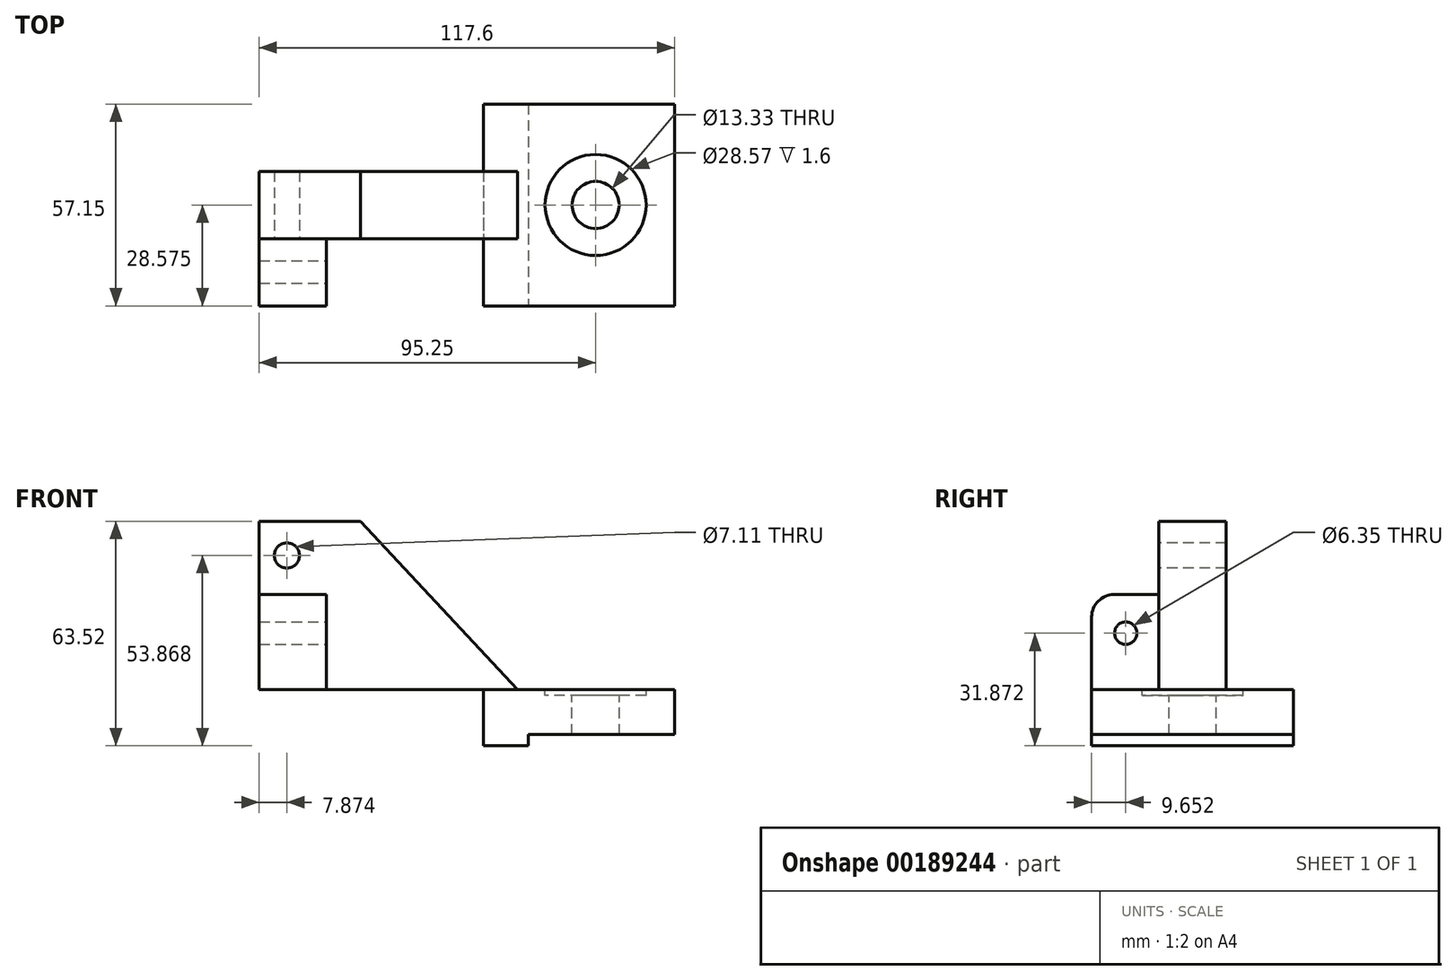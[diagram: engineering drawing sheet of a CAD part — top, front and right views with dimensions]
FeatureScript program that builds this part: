
annotation { "Feature Type Name" : "Feature", "Feature Type Description" : "" }
export const myFeature = defineFeature(function(context is Context, id is Id, definition is map)
    precondition{}
    {
        {
            var Q0;
            Q0=qCreatedBy(makeId("Front.planeOp"),FACE);
            var sketch = newSketch(context, id + "F0", { "sketchPlane" : qUnion([Q0])});
            skLineSegment(sketch, "E0.bottom", {"start": v(0, 0) * mm, "end": v(41.4, 0) * mm});
            skLineSegment(sketch, "E0.top", {"start": v(0, 12.7) * mm, "end": v(41.4, 12.7) * mm});
            skLineSegment(sketch, "E0.left", {"start": v(0, 0) * mm, "end": v(0, 12.7) * mm});
            skLineSegment(sketch, "E0.right", {"start": v(41.4, 0) * mm, "end": v(41.4, 12.7) * mm});
            skLineSegment(sketch, "E1.bottom", {"start": v(0, 12.7) * mm, "end": v(-12.7, 12.7) * mm});
            skLineSegment(sketch, "E1.top", {"start": v(0, -3.17) * mm, "end": v(-12.7, -3.17) * mm});
            skLineSegment(sketch, "E1.left", {"start": v(0, 12.7) * mm, "end": v(0, -3.17) * mm});
            skLineSegment(sketch, "E1.right", {"start": v(-12.7, 12.7) * mm, "end": v(-12.7, -3.18) * mm});
            skSolve(sketch);
        }
        {
            var Q0;
            Q0 = qSketchRegion(id + "F0", true);
            extrude(context, id + "F1", {"entities" : qUnion([Q0]), "oppositeDirection" : true, "depth" : 57.15 * mm});
        }
        {
            var Q0;
            Q0=makeQuery(id+"F1.opExtrude","SWEPT_FACE",FACE,{"disambiguationData":[OSD([sQuery(id+"F0.wireOp",EDGE,"E0.top"),sQuery(id+"F0.wireOp",EDGE,"E1.bottom")])]});
            var sketch = newSketch(context, id + "F2", { "sketchPlane" : qUnion([Q0])});
            skLineSegment(sketch, "E2", {"start": v(41.4, 28.58) * mm, "end": v(41.4, 0) * mm});
            skLineSegment(sketch, "E3", {"start": v(41.4, 28.58) * mm, "end": v(19.05, 28.58) * mm});
            skPoint(sketch, "E4", {"position": v(19.05, 28.58) * mm});
            skLineSegment(sketch, "E5", {"start": v(41.4, 28.58) * mm, "end": v(-3.05, 28.58) * mm});
            skLineSegment(sketch, "E6.bottom", {"start": v(-3.05, 19.05) * mm, "end": v(-47.5, 19.05) * mm});
            skLineSegment(sketch, "E6.top", {"start": v(-3.05, 38.1) * mm, "end": v(-47.5, 38.1) * mm});
            skLineSegment(sketch, "E6.left", {"start": v(-3.05, 19.05) * mm, "end": v(-3.05, 38.1) * mm});
            skLineSegment(sketch, "E6.right", {"start": v(-47.5, 19.05) * mm, "end": v(-47.5, 38.1) * mm});
            skSolve(sketch);
        }
        {
            var Q0;
            Q0=sQuery(id+"F2.wireOp",VERTEX,"E4");
            var Q1;
            Q1=makeQuery(id+"F1.opExtrude","SWEPT_BODY",BODY,{"disambiguationData":[OSD([sQuery(id+"F0.wireOp",EDGE,"E0.bottom"),sQuery(id+"F0.wireOp",EDGE,"E0.top"),sQuery(id+"F0.wireOp",EDGE,"E0.right"),sQuery(id+"F0.wireOp",EDGE,"E1.bottom"),sQuery(id+"F0.wireOp",EDGE,"E1.top"),sQuery(id+"F0.wireOp",EDGE,"E1.left"),sQuery(id+"F0.wireOp",EDGE,"E1.right")])]});
            hole(context, id + "F3", {"style" : HoleStyle.C_BORE, "endStyle" : HoleEndStyle.THROUGH, "standardTappedOrClearance" : lookupTablePath({ "standard" : "ANSI", "fit" : "Normal (ASME)", "size" : "1/4", "type" : "Clearance" }), "standardBlindInLast" : lookupTablePath({ "fit" : "Free", "standard" : "ANSI", "size" : "1/4", "type" : "Clearance" }), "holeDiameter" : 13.33 * mm, "cBoreDiameter" : 28.57 * mm, "cBoreDepth" : 1.6 * mm, "startFromSketch" : true, "locations" : qUnion([Q0]), "scope" : qUnion([Q1]), "isTappedThrough" : true});
        }
        {
            var Q0;
            {var subQ0=sQuery(id+"F2.wireOp",EDGE,"E6.right");Q0=makeQuery(id+"F2.imprint","IMPRINT",FACE,{"disambiguationData":[TD([[makeQuery(id+"F2.imprint","IMPRINT",EDGE,{"derivedFrom":subQ0}),-1.0]])]});}
            var Q1;
            {var subQ0=sQuery(id+"F2.wireOp",EDGE,"E6.left");var subQ1=makeQuery(id+"F2.imprint","INTERSECT",VERTEX,{"derivedFrom":[sQuery(id+"F2.wireOp",EDGE,"E5"),subQ0]});Q1=makeQuery(id+"F2.imprint","IMPRINT",FACE,{"disambiguationData":[TD([[makeQuery(id+"F2.imprint","IMPRINT",EDGE,{"disambiguationData":[TD([[subQ1,1.0]])],"derivedFrom":subQ0}),1.0]])]});}
            extrude(context, id + "F4", {"entities" : qUnion([Q0, Q1]), "operationType" : NewBodyOperationType.ADD, "depth" : 47.65 * mm});
        }
        {
            var Q0;
            Q0=makeQuery(id+"F4.opExtrude","SWEPT_FACE",FACE,{"disambiguationData":[OSD([sQuery(id+"F2.wireOp",EDGE,"E6.bottom")])]});
            var sketch = newSketch(context, id + "F5", { "sketchPlane" : qUnion([Q0])});
            skLineSegment(sketch, "E7", {"start": v(-47.5, 60.35) * mm, "end": v(-3.05, 12.7) * mm});
            skLineSegment(sketch, "E8", {"start": v(-3.05, 12.7) * mm, "end": v(-3.05, 60.35) * mm});
            skLineSegment(sketch, "E9", {"start": v(-3.05, 60.35) * mm, "end": v(-47.5, 60.35) * mm});
            skSolve(sketch);
        }
        {
            var Q0;
            Q0 = qSketchRegion(id + "F5", true);
            extrude(context, id + "F6", {"entities" : qUnion([Q0]), "operationType" : NewBodyOperationType.REMOVE, "oppositeDirection" : true, "depth" : 34.95 * mm});
        }
        {
            var Q0;
            Q0=makeQuery(id+"F4.opExtrude","SWEPT_FACE",FACE,{"disambiguationData":[OSD([sQuery(id+"F2.wireOp",EDGE,"E6.right")])]});
            var sketch = newSketch(context, id + "F7", { "sketchPlane" : qUnion([Q0])});
            skLineSegment(sketch, "E10.bottom", {"start": v(-19.05, 12.7) * mm, "end": v(-38.1, 12.7) * mm});
            skLineSegment(sketch, "E10.top", {"start": v(-19.05, 60.35) * mm, "end": v(-38.1, 60.35) * mm});
            skLineSegment(sketch, "E10.left", {"start": v(-19.05, 12.7) * mm, "end": v(-19.05, 60.35) * mm});
            skLineSegment(sketch, "E10.right", {"start": v(-38.1, 12.7) * mm, "end": v(-38.1, 60.35) * mm});
            skSolve(sketch);
        }
        {
            var Q0;
            Q0 = qSketchRegion(id + "F7", true);
            extrude(context, id + "F8", {"entities" : qUnion([Q0]), "operationType" : NewBodyOperationType.ADD, "depth" : 28.7 * mm});
        }
        {
            var Q0;
            Q0=makeQuery(id+"F8.boolean.opBoolean","MERGE",FACE,{"derivedFrom":[makeQuery(id+"F4.opExtrude","SWEPT_FACE",FACE,{"disambiguationData":[OSD([sQuery(id+"F2.wireOp",EDGE,"E6.bottom")])]}),makeQuery(id+"F8.opExtrude","SWEPT_FACE",FACE,{"disambiguationData":[OSD([sQuery(id+"F7.wireOp",EDGE,"E10.left")])]})]});
            var sketch = newSketch(context, id + "F9", { "sketchPlane" : qUnion([Q0])});
            skLineSegment(sketch, "E11.bottom", {"start": v(-76.2, 12.7) * mm, "end": v(-57.15, 12.7) * mm});
            skLineSegment(sketch, "E11.top", {"start": v(-76.2, 39.62) * mm, "end": v(-57.15, 39.62) * mm});
            skLineSegment(sketch, "E11.left", {"start": v(-76.2, 12.7) * mm, "end": v(-76.2, 39.62) * mm});
            skLineSegment(sketch, "E11.right", {"start": v(-57.15, 12.7) * mm, "end": v(-57.15, 39.62) * mm});
            skSolve(sketch);
        }
        {
            var Q0;
            Q0 = qSketchRegion(id + "F9", true);
            extrude(context, id + "F10", {"entities" : qUnion([Q0]), "operationType" : NewBodyOperationType.ADD, "depth" : 19.05 * mm});
        }
        {
            var Q0;
            Q0=makeQuery(id+"F10.opExtrude","CAP_EDGE",EDGE,{"disambiguationData":[OSD([sQuery(id+"F9.wireOp",EDGE,"E11.top")])],"isStart":false});
            fillet(context, id + "F11", {"entities" : qUnion([Q0]), "radius" : 6.35 * mm, "tangentPropagation" : true, "allowEdgeOverflow" : false});
        }
        {
            var Q0;
            Q0=makeQuery(id+"F10.opExtrude","SWEPT_FACE",FACE,{"disambiguationData":[OSD([sQuery(id+"F9.wireOp",EDGE,"E11.right")])]});
            var sketch = newSketch(context, id + "F12", { "sketchPlane" : qUnion([Q0])});
            skLineSegment(sketch, "E12.bottom", {"start": v(0, 12.7) * mm, "end": v(9.65, 12.7) * mm});
            skLineSegment(sketch, "E12.top", {"start": v(0, 28.7) * mm, "end": v(9.65, 28.7) * mm});
            skLineSegment(sketch, "E12.left", {"start": v(0, 12.7) * mm, "end": v(0, 28.7) * mm});
            skLineSegment(sketch, "E12.right", {"start": v(9.65, 12.7) * mm, "end": v(9.65, 28.7) * mm});
            skPoint(sketch, "E13", {"position": v(9.65, 28.7) * mm});
            skSolve(sketch);
        }
        {
            var Q0;
            Q0=makeQuery(id+"F8.boolean.opBoolean","MERGE",FACE,{"derivedFrom":[makeQuery(id+"F4.opExtrude","SWEPT_FACE",FACE,{"disambiguationData":[OSD([sQuery(id+"F2.wireOp",EDGE,"E6.bottom")])]}),makeQuery(id+"F8.opExtrude","SWEPT_FACE",FACE,{"disambiguationData":[OSD([sQuery(id+"F7.wireOp",EDGE,"E10.left")])]})]});
            var sketch = newSketch(context, id + "F13", { "sketchPlane" : qUnion([Q0])});
            skLineSegment(sketch, "E14.bottom", {"start": v(-76.2, 60.35) * mm, "end": v(-68.33, 60.35) * mm});
            skLineSegment(sketch, "E14.top", {"start": v(-76.2, 50.7) * mm, "end": v(-68.33, 50.7) * mm});
            skLineSegment(sketch, "E14.left", {"start": v(-76.2, 60.35) * mm, "end": v(-76.2, 50.7) * mm});
            skLineSegment(sketch, "E14.right", {"start": v(-68.33, 60.35) * mm, "end": v(-68.33, 50.7) * mm});
            skPoint(sketch, "E15", {"position": v(-68.33, 50.7) * mm});
            skSolve(sketch);
        }
        {
            var Q0;
            Q0=sQuery(id+"F12.wireOp",VERTEX,"E13");
            var Q1;
            Q1=makeQuery(id+"F1.opExtrude","SWEPT_BODY",BODY,{"disambiguationData":[OSD([sQuery(id+"F0.wireOp",EDGE,"E0.bottom"),sQuery(id+"F0.wireOp",EDGE,"E0.top"),sQuery(id+"F0.wireOp",EDGE,"E0.right"),sQuery(id+"F0.wireOp",EDGE,"E1.bottom"),sQuery(id+"F0.wireOp",EDGE,"E1.top"),sQuery(id+"F0.wireOp",EDGE,"E1.left"),sQuery(id+"F0.wireOp",EDGE,"E1.right")])]});
            hole(context, id + "F14", {"style" : HoleStyle.SIMPLE, "endStyle" : HoleEndStyle.THROUGH, "holeDiameter" : 6.35 * mm, "startFromSketch" : true, "locations" : qUnion([Q0]), "scope" : qUnion([Q1]), "isTappedThrough" : true});
        }
        {
            var Q0;
            Q0=sQuery(id+"F13.wireOp",VERTEX,"E15");
            var Q1;
            Q1=makeQuery(id+"F1.opExtrude","SWEPT_BODY",BODY,{"disambiguationData":[OSD([sQuery(id+"F0.wireOp",EDGE,"E0.bottom"),sQuery(id+"F0.wireOp",EDGE,"E0.top"),sQuery(id+"F0.wireOp",EDGE,"E0.right"),sQuery(id+"F0.wireOp",EDGE,"E1.bottom"),sQuery(id+"F0.wireOp",EDGE,"E1.top"),sQuery(id+"F0.wireOp",EDGE,"E1.left"),sQuery(id+"F0.wireOp",EDGE,"E1.right")])]});
            hole(context, id + "F15", {"style" : HoleStyle.SIMPLE, "endStyle" : HoleEndStyle.THROUGH, "standardTappedOrClearance" : lookupTablePath({ "standard" : "ANSI", "fit" : "Normal (ASME)", "size" : "1/4", "type" : "Clearance" }), "standardBlindInLast" : lookupTablePath({ "fit" : "Free", "standard" : "ANSI", "size" : "1/4", "type" : "Clearance" }), "holeDiameter" : 7.11 * mm, "startFromSketch" : true, "locations" : qUnion([Q0]), "scope" : qUnion([Q1]), "isTappedThrough" : true});
        }
    });
